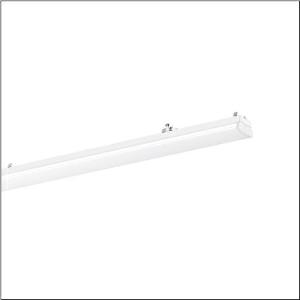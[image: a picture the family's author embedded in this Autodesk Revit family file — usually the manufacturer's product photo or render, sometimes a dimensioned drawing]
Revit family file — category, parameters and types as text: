
# Revit family: licross_r__21_recessed_opal_mo_52tl1ddn495g_bbb7
name_source: partatom
category: Lighting Fixtures
units: mm (PartAtom-declared; Revit-internal decimal feet)

## family parameters
Cut with Voids When Loaded = No
Host = Face
Light Source = No
Part Type = Normal
Room Calculation Point = No
Round Connector Dimension = Use Diameter
Shared = No

## types (1)
- --- (1 x LED, 9740 lm, 58 W, 4000K)
    Apparent Load = 58 VA
    CIE Flux Codes = 44 73 91 87 100
    Color Rendering = 80
    Color Temperature = 4000K
    Default Elevation = 1800 mm
    Description = Licross® 21 recessed opal MO, luminaire insert, of sheet steel, galvanised, coil coated, white, length: 1.500mm, width: 66mm, height: 67mm, LED rated luminous flux: 9.750lm, light colour: 840, control gear: DALI 2, with plug, 5-pole, with phase selection, mains connection: 220..240V, AC, 50/60Hz, rated input power: 58W, halogen-free wiring, primary optical cover: cover, of PMMA, light emission: direct with ceiling illumination distribution, primary light characteristic: symmetric, protection rating (complete): IP40, insulation class (complete): insulation class I (protective earthing), certification: CE, ENEC, VDE, UKCA, protection symbol: D if used in an environment without relevant dust loads with corresponding accessories, impact resistance: IK06, permissible ambient temperature for indoor applications: -25..+35°C, corresponds to IFS (International Featured Standards) requirements for safety and quality in the food industry, reducing of maximum allowable ambient temperature of 5°C with ceiling mounting, LABS conformity tested according to VDMA 24364:2018-05, packaging unit: 1 piece
    Height = 83 mm
    Lamp = 1 x LED
    Lamp Light Flux = 9740 lm
    Lamp Power = 58 W
    Lamp count = 1
    Length = 1500 mm
    Luminous efficacy = 168 lm/W
    Manufacturer = Siteco
    ModVariant = No
    Model = 52TL1DDN495G
    Mounting Place = Ceiling
    Mounting Type = Pendant
    Number of Poles = 1
    OnlyDefault = Yes
    Power Factor = 1
    Product Name = Licross® 21 recessed opal MO
    Product group = luminaire insert
    ProductGroupID = 901
    Protection Class = Protection class I
    Protection Degree = IP 40
    RLX_Detail_Level = 1
    RLX_Emergency_Light_Flux = 0 lm
    RLX_Emergency_Type = 0
    RLX_Emergency_Type_DB = No
    RlxData = <blob elided: 26921 chars, md5=8a0c772d>
    Socket = socket
    Standby Power = 0 W
    System Light Flux = 9740 lm
    System Power = 58 W
    Type Comments = factory setting: luminous flux: 100 % | dim-lin: 254 | 390 mA
    Type Image = l_1313666.jpg
    URL = http://relux.com
    VarID = @adj_027173
    Voltage = 0 V
    Weight = 0.00 kg
    Width = 76 mm

## geometry (parser evidence)
native form markers: Blend x4, Sweep x12
no freeform markers — native parametric forms only
